# Revit family: SURE-BOARD-SERIES200
name_source: partatom
category: Generic Models
units: mm (PartAtom-declared; Revit-internal decimal feet)

## family parameters
Can host rebar = No
Cut with Voids When Loaded = No
Host = Face
Maintain Annotation Orientation = No
Part Type = Normal
Room Calculation Point = No
Round Connector Dimension = Use Diameter
Shared = No

## types (3) — shared parameters
Default Elevation = 4' - 0"
Manufacturer = California  Expanded Metal Lath Products Co. (CEMCO)
Product Submittal Link = https://cemcosteel.com
SteelSheetThickness = 0' - 0 1/32"
URL = http://www.cemcosteel.com
Width = 4' - 0"

## per-type parameters (varying)
| type | Assembly Code | Description | Keynote | Model | Product Info | Wallboard Thickness |
| SureBoard200-50 | B1010220 | Sure-Board® Series 200 for Steel Framing | 054000 |  | Sure-Board® Series 200W for Wood Framing | 0' - 0 1/2" |
| SureBoard200-62 |  | Sure-Board® Series 200 for Steel Framing is a steel sheet and gypsum board composite product that is installed on steel framed shearwalls at points requiring shear. |  |  | Sure-Board® Series 200 for Cold-Formed Steel Framing | 0' - 0 5/8" |
| SureBoard200-75 | B10 | Sure-Board® Series 200 for Steel Framing is a steel sheet and gypsum board composite product that is installed on steel framed shearwalls at points requiring shear. |  | V1 | Sure-Board® Series 200 for Cold-Formed Steel Framing | 0' - 0 3/4" |

## geometry (parser evidence)
native form markers: Sweep x2
no freeform markers — native parametric forms only
